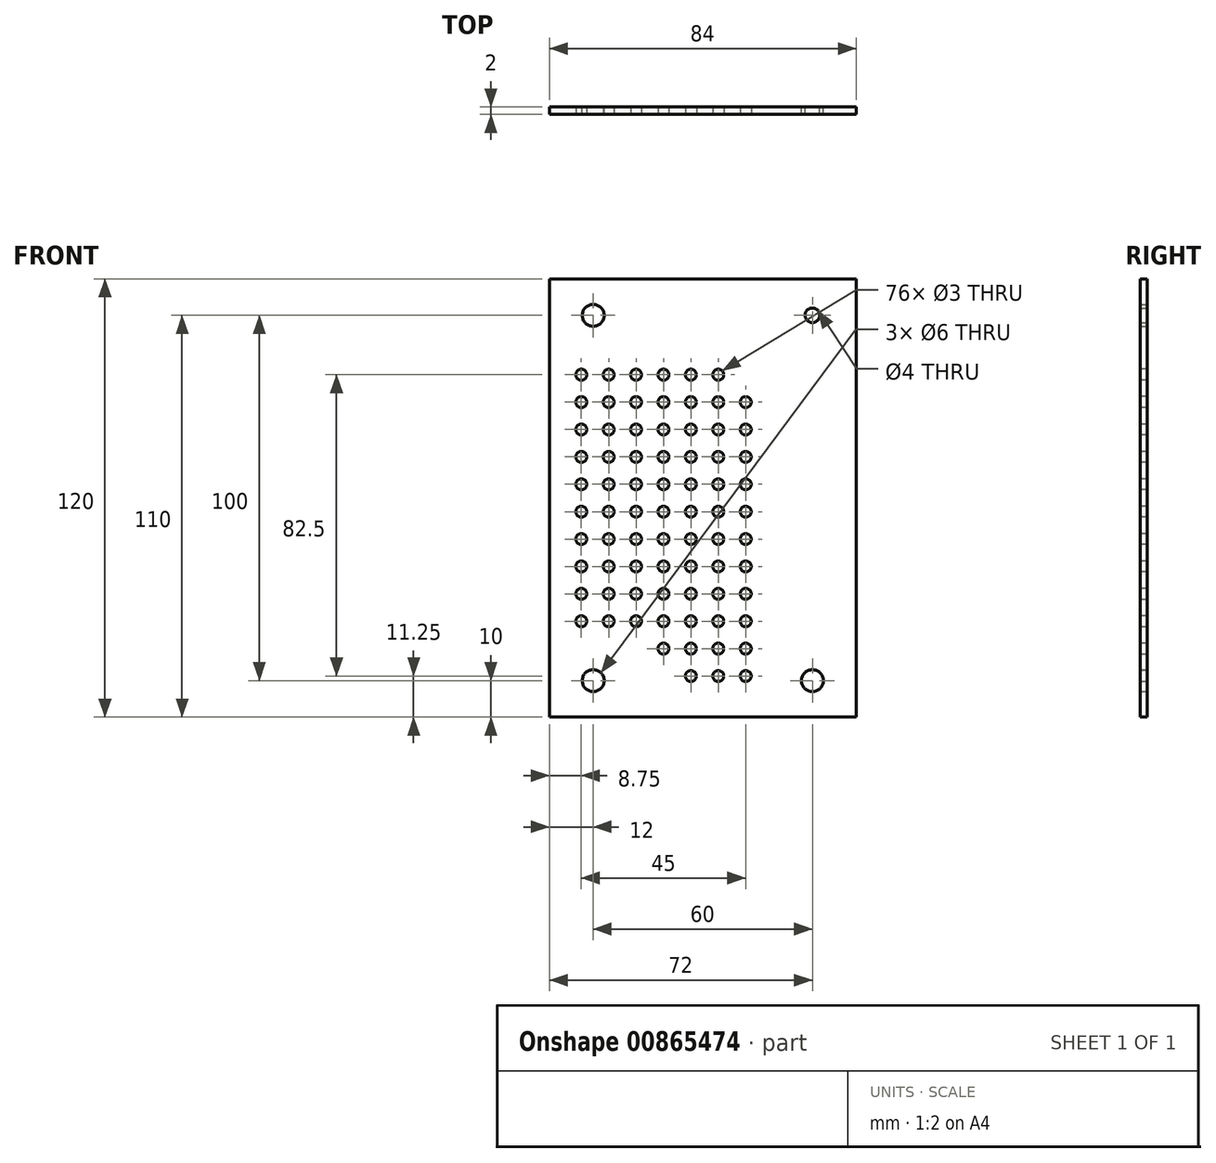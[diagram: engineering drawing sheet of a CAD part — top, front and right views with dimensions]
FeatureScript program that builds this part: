
annotation { "Feature Type Name" : "Feature", "Feature Type Description" : "" }
export const myFeature = defineFeature(function(context is Context, id is Id, definition is map)
    precondition{}
    {
        {
            var Q0;
            Q0=qCreatedBy(makeId("Front.planeOp"),FACE);
            var sketch = newSketch(context, id + "F0", { "sketchPlane" : qUnion([Q0])});
            skLineSegment(sketch, "E0.bottom", {"start": v(42, 60) * mm, "end": v(-42, 60) * mm});
            skLineSegment(sketch, "E0.top", {"start": v(42, -60) * mm, "end": v(-42, -60) * mm});
            skLineSegment(sketch, "E0.left", {"start": v(42, 60) * mm, "end": v(42, -60) * mm});
            skLineSegment(sketch, "E0.right", {"start": v(-42, 60) * mm, "end": v(-42, -60) * mm});
            skPoint(sketch, "E0.middle", {"position": v(0, 0) * mm});
            skCircle(sketch, "E1", {"center": v(-30, 50) * mm, "radius": 3 * mm});
            skCircle(sketch, "E2", {"center": v(30, 50) * mm, "radius": 2 * mm});
            skCircle(sketch, "E3", {"center": v(30, -50) * mm, "radius": 3 * mm});
            skCircle(sketch, "E4", {"center": v(-30, -50) * mm, "radius": 3 * mm});
            skSolve(sketch);
        }
        {
            var Q0;
            Q0=qSketchRegion(id+"F0",true);
            extrude(context, id + "F1", {"entities" : qUnion([Q0]), "depth" : 2 * mm, "offsetDistance" : 25 * mm});
        }
        {
            var Q0;
            Q0=makeQuery(id+"F1.opExtrude","CAP_FACE",FACE,{"disambiguationData":[OSD([sQuery(id+"F0.wireOp",EDGE,"E0.bottom"),sQuery(id+"F0.wireOp",EDGE,"E0.top"),sQuery(id+"F0.wireOp",EDGE,"E0.left"),sQuery(id+"F0.wireOp",EDGE,"E0.right"),sQuery(id+"F0.wireOp",EDGE,"E1"),sQuery(id+"F0.wireOp",EDGE,"E2"),sQuery(id+"F0.wireOp",EDGE,"E3"),sQuery(id+"F0.wireOp",EDGE,"E4")])],"isStart":false});
            var sketch = newSketch(context, id + "F2", { "sketchPlane" : qUnion([Q0])});
            skCircle(sketch, "E5", {"center": v(-33.25, 33.75) * mm, "radius": 1.5 * mm});
            skCircle(sketch, "E6.0.1.0", {"center": v(-33.25, 26.25) * mm, "radius": 1.5 * mm});
            skCircle(sketch, "E6.0.2.0", {"center": v(-33.25, 18.75) * mm, "radius": 1.5 * mm});
            skCircle(sketch, "E6.0.3.0", {"center": v(-33.25, 11.25) * mm, "radius": 1.5 * mm});
            skCircle(sketch, "E6.0.4.0", {"center": v(-33.25, 3.75) * mm, "radius": 1.5 * mm});
            skCircle(sketch, "E6.0.5.0", {"center": v(-33.25, -3.75) * mm, "radius": 1.5 * mm});
            skCircle(sketch, "E6.0.6.0", {"center": v(-33.25, -11.25) * mm, "radius": 1.5 * mm});
            skCircle(sketch, "E6.0.7.0", {"center": v(-33.25, -18.75) * mm, "radius": 1.5 * mm});
            skCircle(sketch, "E6.0.8.0", {"center": v(-33.25, -26.25) * mm, "radius": 1.5 * mm});
            skCircle(sketch, "E6.0.9.0", {"center": v(-33.25, -33.75) * mm, "radius": 1.5 * mm});
            skCircle(sketch, "E6.1.0.0", {"center": v(-25.75, 33.75) * mm, "radius": 1.5 * mm});
            skCircle(sketch, "E6.1.1.0", {"center": v(-25.75, 26.25) * mm, "radius": 1.5 * mm});
            skCircle(sketch, "E6.1.2.0", {"center": v(-25.75, 18.75) * mm, "radius": 1.5 * mm});
            skCircle(sketch, "E6.1.3.0", {"center": v(-25.75, 11.25) * mm, "radius": 1.5 * mm});
            skCircle(sketch, "E6.1.4.0", {"center": v(-25.75, 3.75) * mm, "radius": 1.5 * mm});
            skCircle(sketch, "E6.1.5.0", {"center": v(-25.75, -3.75) * mm, "radius": 1.5 * mm});
            skCircle(sketch, "E6.1.6.0", {"center": v(-25.75, -11.25) * mm, "radius": 1.5 * mm});
            skCircle(sketch, "E6.1.7.0", {"center": v(-25.75, -18.75) * mm, "radius": 1.5 * mm});
            skCircle(sketch, "E6.1.8.0", {"center": v(-25.75, -26.25) * mm, "radius": 1.5 * mm});
            skCircle(sketch, "E6.1.9.0", {"center": v(-25.75, -33.75) * mm, "radius": 1.5 * mm});
            skCircle(sketch, "E6.2.0.0", {"center": v(-18.25, 33.75) * mm, "radius": 1.5 * mm});
            skCircle(sketch, "E6.2.1.0", {"center": v(-18.25, 26.25) * mm, "radius": 1.5 * mm});
            skCircle(sketch, "E6.2.2.0", {"center": v(-18.25, 18.75) * mm, "radius": 1.5 * mm});
            skCircle(sketch, "E6.2.3.0", {"center": v(-18.25, 11.25) * mm, "radius": 1.5 * mm});
            skCircle(sketch, "E6.2.4.0", {"center": v(-18.25, 3.75) * mm, "radius": 1.5 * mm});
            skCircle(sketch, "E6.2.5.0", {"center": v(-18.25, -3.75) * mm, "radius": 1.5 * mm});
            skCircle(sketch, "E6.2.6.0", {"center": v(-18.25, -11.25) * mm, "radius": 1.5 * mm});
            skCircle(sketch, "E6.2.7.0", {"center": v(-18.25, -18.75) * mm, "radius": 1.5 * mm});
            skCircle(sketch, "E6.2.8.0", {"center": v(-18.25, -26.25) * mm, "radius": 1.5 * mm});
            skCircle(sketch, "E6.2.9.0", {"center": v(-18.25, -33.75) * mm, "radius": 1.5 * mm});
            skCircle(sketch, "E6.3.0.0", {"center": v(-10.75, 33.75) * mm, "radius": 1.5 * mm});
            skCircle(sketch, "E6.3.1.0", {"center": v(-10.75, 26.25) * mm, "radius": 1.5 * mm});
            skCircle(sketch, "E6.3.2.0", {"center": v(-10.75, 18.75) * mm, "radius": 1.5 * mm});
            skCircle(sketch, "E6.3.3.0", {"center": v(-10.75, 11.25) * mm, "radius": 1.5 * mm});
            skCircle(sketch, "E6.3.4.0", {"center": v(-10.75, 3.75) * mm, "radius": 1.5 * mm});
            skCircle(sketch, "E6.3.5.0", {"center": v(-10.75, -3.75) * mm, "radius": 1.5 * mm});
            skCircle(sketch, "E6.3.6.0", {"center": v(-10.75, -11.25) * mm, "radius": 1.5 * mm});
            skCircle(sketch, "E6.3.7.0", {"center": v(-10.75, -18.75) * mm, "radius": 1.5 * mm});
            skCircle(sketch, "E6.3.8.0", {"center": v(-10.75, -26.25) * mm, "radius": 1.5 * mm});
            skCircle(sketch, "E6.3.9.0", {"center": v(-10.75, -33.75) * mm, "radius": 1.5 * mm});
            skCircle(sketch, "E6.4.0.0", {"center": v(-3.25, 33.75) * mm, "radius": 1.5 * mm});
            skCircle(sketch, "E6.4.1.0", {"center": v(-3.25, 26.25) * mm, "radius": 1.5 * mm});
            skCircle(sketch, "E6.4.2.0", {"center": v(-3.25, 18.75) * mm, "radius": 1.5 * mm});
            skCircle(sketch, "E6.4.3.0", {"center": v(-3.25, 11.25) * mm, "radius": 1.5 * mm});
            skCircle(sketch, "E6.4.4.0", {"center": v(-3.25, 3.75) * mm, "radius": 1.5 * mm});
            skCircle(sketch, "E6.4.5.0", {"center": v(-3.25, -3.75) * mm, "radius": 1.5 * mm});
            skCircle(sketch, "E6.4.6.0", {"center": v(-3.25, -11.25) * mm, "radius": 1.5 * mm});
            skCircle(sketch, "E6.4.7.0", {"center": v(-3.25, -18.75) * mm, "radius": 1.5 * mm});
            skCircle(sketch, "E6.4.8.0", {"center": v(-3.25, -26.25) * mm, "radius": 1.5 * mm});
            skCircle(sketch, "E6.4.9.0", {"center": v(-3.25, -33.75) * mm, "radius": 1.5 * mm});
            skCircle(sketch, "E6.5.0.0", {"center": v(4.25, 33.75) * mm, "radius": 1.5 * mm});
            skCircle(sketch, "E6.5.1.0", {"center": v(4.25, 26.25) * mm, "radius": 1.5 * mm});
            skCircle(sketch, "E6.5.2.0", {"center": v(4.25, 18.75) * mm, "radius": 1.5 * mm});
            skCircle(sketch, "E6.5.3.0", {"center": v(4.25, 11.25) * mm, "radius": 1.5 * mm});
            skCircle(sketch, "E6.5.4.0", {"center": v(4.25, 3.75) * mm, "radius": 1.5 * mm});
            skCircle(sketch, "E6.5.5.0", {"center": v(4.25, -3.75) * mm, "radius": 1.5 * mm});
            skCircle(sketch, "E6.5.6.0", {"center": v(4.25, -11.25) * mm, "radius": 1.5 * mm});
            skCircle(sketch, "E6.5.7.0", {"center": v(4.25, -18.75) * mm, "radius": 1.5 * mm});
            skCircle(sketch, "E6.5.8.0", {"center": v(4.25, -26.25) * mm, "radius": 1.5 * mm});
            skCircle(sketch, "E6.5.9.0", {"center": v(4.25, -33.75) * mm, "radius": 1.5 * mm});
            skCircle(sketch, "E6.6.1.0", {"center": v(11.75, 26.25) * mm, "radius": 1.5 * mm});
            skCircle(sketch, "E6.6.2.0", {"center": v(11.75, 18.75) * mm, "radius": 1.5 * mm});
            skCircle(sketch, "E6.6.3.0", {"center": v(11.75, 11.25) * mm, "radius": 1.5 * mm});
            skCircle(sketch, "E6.6.4.0", {"center": v(11.75, 3.75) * mm, "radius": 1.5 * mm});
            skCircle(sketch, "E6.6.5.0", {"center": v(11.75, -3.75) * mm, "radius": 1.5 * mm});
            skCircle(sketch, "E6.6.6.0", {"center": v(11.75, -11.25) * mm, "radius": 1.5 * mm});
            skCircle(sketch, "E6.6.7.0", {"center": v(11.75, -18.75) * mm, "radius": 1.5 * mm});
            skCircle(sketch, "E6.6.8.0", {"center": v(11.75, -26.25) * mm, "radius": 1.5 * mm});
            skCircle(sketch, "E6.6.9.0", {"center": v(11.75, -33.75) * mm, "radius": 1.5 * mm});
            skLineSegment(sketch, "E6.direction1", {"start": v(-33.25, 33.75) * mm, "end": v(-25.75, 33.75) * mm, "construction": true});
            skLineSegment(sketch, "E6.direction2", {"start": v(-33.25, 33.75) * mm, "end": v(-33.25, 26.25) * mm, "construction": true});
            skSolve(sketch);
        }
        {
            var Q0;
            Q0 = qSketchRegion(id + "F2", true);
            extrude(context, id + "F3", {"entities" : qUnion([Q0]), "operationType" : NewBodyOperationType.REMOVE, "endBound" : BoundingType.THROUGH_ALL, "oppositeDirection" : true, "depth" : 25 * mm, "offsetDistance" : 25 * mm});
        }
        {
            var Q0;
            Q0=makeQuery(id+"F1.opExtrude","CAP_FACE",FACE,{"disambiguationData":[OSD([sQuery(id+"F0.wireOp",EDGE,"E0.bottom"),sQuery(id+"F0.wireOp",EDGE,"E0.top"),sQuery(id+"F0.wireOp",EDGE,"E0.left"),sQuery(id+"F0.wireOp",EDGE,"E0.right"),sQuery(id+"F0.wireOp",EDGE,"E1"),sQuery(id+"F0.wireOp",EDGE,"E2"),sQuery(id+"F0.wireOp",EDGE,"E3"),sQuery(id+"F0.wireOp",EDGE,"E4")])],"isStart":false});
            var sketch = newSketch(context, id + "F4", { "sketchPlane" : qUnion([Q0])});
            skLineSegment(sketch, "E7", {"start": v(11.75, -33.75) * mm, "end": v(11.75, -46.92) * mm});
            skCircle(sketch, "E8", {"center": v(11.75, -41.25) * mm, "radius": 1.5 * mm});
            skCircle(sketch, "E9.0.1.0", {"center": v(11.75, -48.75) * mm, "radius": 1.5 * mm});
            skCircle(sketch, "E9.1.0.0", {"center": v(4.25, -41.25) * mm, "radius": 1.5 * mm});
            skCircle(sketch, "E9.1.1.0", {"center": v(4.25, -48.75) * mm, "radius": 1.5 * mm});
            skCircle(sketch, "E9.2.0.0", {"center": v(-3.25, -41.25) * mm, "radius": 1.5 * mm});
            skCircle(sketch, "E9.2.1.0", {"center": v(-3.25, -48.75) * mm, "radius": 1.5 * mm});
            skLineSegment(sketch, "E9.direction1", {"start": v(11.75, -41.25) * mm, "end": v(4.25, -41.25) * mm, "construction": true});
            skLineSegment(sketch, "E9.direction2", {"start": v(11.75, -41.25) * mm, "end": v(11.75, -48.75) * mm, "construction": true});
            skCircle(sketch, "E10.0.3.0", {"center": v(-10.75, -41.25) * mm, "radius": 1.5 * mm});
            skSolve(sketch);
        }
        {
            var Q0;
            Q0 = qSketchRegion(id + "F4", true);
            extrude(context, id + "F5", {"entities" : qUnion([Q0]), "operationType" : NewBodyOperationType.REMOVE, "endBound" : BoundingType.THROUGH_ALL, "oppositeDirection" : true, "depth" : 25 * mm, "offsetDistance" : 25 * mm});
        }
    });
